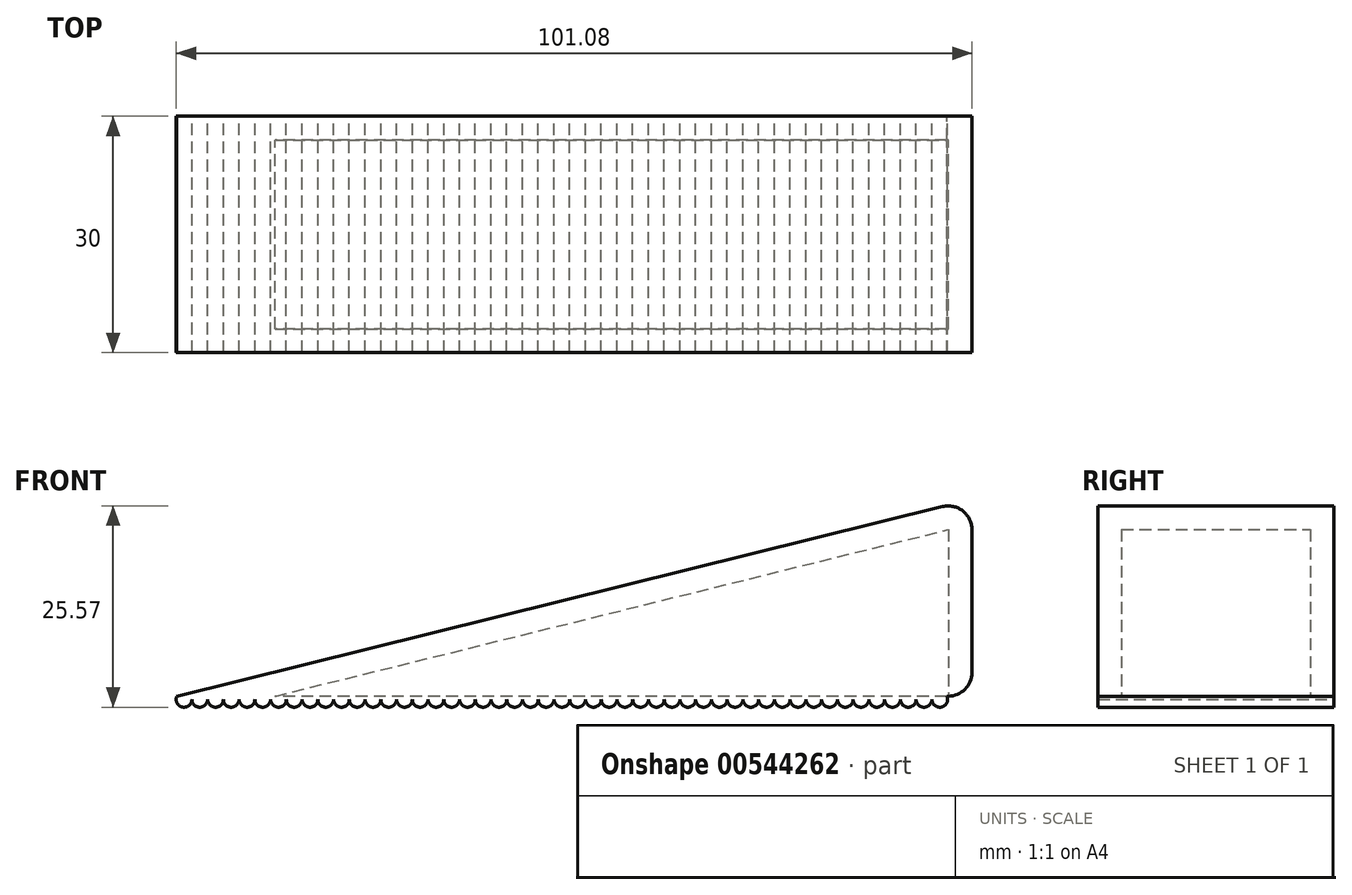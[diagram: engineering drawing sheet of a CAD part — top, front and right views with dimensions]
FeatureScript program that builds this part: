
annotation { "Feature Type Name" : "Feature", "Feature Type Description" : "" }
export const myFeature = defineFeature(function(context is Context, id is Id, definition is map)
    precondition{}
    {
        {
            var Q0;
            Q0=qCreatedBy(makeId("Front.planeOp"),FACE);
            var sketch = newSketch(context, id + "F0", { "sketchPlane" : qUnion([Q0])});
            skLineSegment(sketch, "E0", {"start": v(-3, 0) * mm, "end": v(-101, 0) * mm});
            skLineSegment(sketch, "E1", {"start": v(-101, 0) * mm, "end": v(-3.72, 24.08) * mm});
            skLineSegment(sketch, "E2", {"start": v(0, 21.17) * mm, "end": v(0, 3) * mm});
            skPoint(sketch, "E3.visualSharp", {"position": v(0, 25) * mm});
            skArc(sketch, "E3.filletArc", {"start": v(0, 21.17) * mm, "mid": v(-1.15, 23.53) * mm, "end": v(-3.72, 24.08) * mm});
            skPoint(sketch, "E4.visualSharp", {"position": v(0, 0) * mm});
            skArc(sketch, "E4.filletArc", {"start": v(-3, 0) * mm, "mid": v(-0.88, 0.88) * mm, "end": v(0, 3) * mm});
            skArc(sketch, "E5", {"start": v(-101, 0) * mm, "mid": v(-100.08, -1.4) * mm, "end": v(-99.17, 0) * mm});
            skArc(sketch, "E6.1.0.0", {"start": v(-99, 0) * mm, "mid": v(-98.08, -1.4) * mm, "end": v(-97.17, 0) * mm});
            skArc(sketch, "E6.2.0.0", {"start": v(-97, 0) * mm, "mid": v(-96.08, -1.4) * mm, "end": v(-95.17, 0) * mm});
            skArc(sketch, "E6.3.0.0", {"start": v(-95, 0) * mm, "mid": v(-94.08, -1.4) * mm, "end": v(-93.17, 0) * mm});
            skArc(sketch, "E6.4.0.0", {"start": v(-93, 0) * mm, "mid": v(-92.08, -1.4) * mm, "end": v(-91.17, 0) * mm});
            skArc(sketch, "E6.5.0.0", {"start": v(-91, 0) * mm, "mid": v(-90.08, -1.4) * mm, "end": v(-89.17, 0) * mm});
            skArc(sketch, "E6.6.0.0", {"start": v(-89, 0) * mm, "mid": v(-88.08, -1.4) * mm, "end": v(-87.17, 0) * mm});
            skArc(sketch, "E6.7.0.0", {"start": v(-87, 0) * mm, "mid": v(-86.08, -1.4) * mm, "end": v(-85.17, 0) * mm});
            skArc(sketch, "E6.8.0.0", {"start": v(-85, 0) * mm, "mid": v(-84.08, -1.4) * mm, "end": v(-83.17, 0) * mm});
            skArc(sketch, "E6.9.0.0", {"start": v(-83, 0) * mm, "mid": v(-82.08, -1.4) * mm, "end": v(-81.17, 0) * mm});
            skArc(sketch, "E6.10.0.0", {"start": v(-81, 0) * mm, "mid": v(-80.08, -1.4) * mm, "end": v(-79.17, 0) * mm});
            skArc(sketch, "E6.11.0.0", {"start": v(-79, 0) * mm, "mid": v(-78.08, -1.4) * mm, "end": v(-77.17, 0) * mm});
            skArc(sketch, "E6.12.0.0", {"start": v(-77, 0) * mm, "mid": v(-76.08, -1.4) * mm, "end": v(-75.17, 0) * mm});
            skArc(sketch, "E6.13.0.0", {"start": v(-75, 0) * mm, "mid": v(-74.08, -1.4) * mm, "end": v(-73.17, 0) * mm});
            skArc(sketch, "E6.14.0.0", {"start": v(-73, 0) * mm, "mid": v(-72.08, -1.4) * mm, "end": v(-71.17, 0) * mm});
            skArc(sketch, "E6.15.0.0", {"start": v(-71, 0) * mm, "mid": v(-70.08, -1.4) * mm, "end": v(-69.17, 0) * mm});
            skArc(sketch, "E6.16.0.0", {"start": v(-69, 0) * mm, "mid": v(-68.08, -1.4) * mm, "end": v(-67.17, 0) * mm});
            skArc(sketch, "E6.17.0.0", {"start": v(-67, 0) * mm, "mid": v(-66.08, -1.4) * mm, "end": v(-65.17, 0) * mm});
            skArc(sketch, "E6.18.0.0", {"start": v(-65, 0) * mm, "mid": v(-64.08, -1.4) * mm, "end": v(-63.17, 0) * mm});
            skArc(sketch, "E6.19.0.0", {"start": v(-63, 0) * mm, "mid": v(-62.08, -1.4) * mm, "end": v(-61.17, 0) * mm});
            skArc(sketch, "E6.20.0.0", {"start": v(-61, 0) * mm, "mid": v(-60.08, -1.4) * mm, "end": v(-59.17, 0) * mm});
            skArc(sketch, "E6.21.0.0", {"start": v(-59, 0) * mm, "mid": v(-58.08, -1.4) * mm, "end": v(-57.17, 0) * mm});
            skArc(sketch, "E6.22.0.0", {"start": v(-57, 0) * mm, "mid": v(-56.08, -1.4) * mm, "end": v(-55.17, 0) * mm});
            skArc(sketch, "E6.23.0.0", {"start": v(-55, 0) * mm, "mid": v(-54.08, -1.4) * mm, "end": v(-53.17, 0) * mm});
            skArc(sketch, "E6.24.0.0", {"start": v(-53, 0) * mm, "mid": v(-52.08, -1.4) * mm, "end": v(-51.17, 0) * mm});
            skArc(sketch, "E6.25.0.0", {"start": v(-51, 0) * mm, "mid": v(-50.08, -1.4) * mm, "end": v(-49.17, 0) * mm});
            skArc(sketch, "E6.26.0.0", {"start": v(-49, 0) * mm, "mid": v(-48.08, -1.4) * mm, "end": v(-47.17, 0) * mm});
            skArc(sketch, "E6.27.0.0", {"start": v(-47, 0) * mm, "mid": v(-46.08, -1.4) * mm, "end": v(-45.17, 0) * mm});
            skArc(sketch, "E6.28.0.0", {"start": v(-45, 0) * mm, "mid": v(-44.08, -1.4) * mm, "end": v(-43.17, 0) * mm});
            skArc(sketch, "E6.29.0.0", {"start": v(-43, 0) * mm, "mid": v(-42.08, -1.4) * mm, "end": v(-41.17, 0) * mm});
            skArc(sketch, "E6.30.0.0", {"start": v(-41, 0) * mm, "mid": v(-40.08, -1.4) * mm, "end": v(-39.17, 0) * mm});
            skArc(sketch, "E6.31.0.0", {"start": v(-39, 0) * mm, "mid": v(-38.08, -1.4) * mm, "end": v(-37.17, 0) * mm});
            skArc(sketch, "E6.32.0.0", {"start": v(-37, 0) * mm, "mid": v(-36.08, -1.4) * mm, "end": v(-35.17, 0) * mm});
            skArc(sketch, "E6.33.0.0", {"start": v(-35, 0) * mm, "mid": v(-34.08, -1.4) * mm, "end": v(-33.17, 0) * mm});
            skArc(sketch, "E6.34.0.0", {"start": v(-33, 0) * mm, "mid": v(-32.08, -1.4) * mm, "end": v(-31.17, 0) * mm});
            skArc(sketch, "E6.35.0.0", {"start": v(-31, 0) * mm, "mid": v(-30.08, -1.4) * mm, "end": v(-29.17, 0) * mm});
            skArc(sketch, "E6.36.0.0", {"start": v(-29, 0) * mm, "mid": v(-28.08, -1.4) * mm, "end": v(-27.17, 0) * mm});
            skArc(sketch, "E6.37.0.0", {"start": v(-27, 0) * mm, "mid": v(-26.08, -1.4) * mm, "end": v(-25.17, 0) * mm});
            skArc(sketch, "E6.38.0.0", {"start": v(-25, 0) * mm, "mid": v(-24.08, -1.4) * mm, "end": v(-23.17, 0) * mm});
            skArc(sketch, "E6.39.0.0", {"start": v(-23, 0) * mm, "mid": v(-22.08, -1.4) * mm, "end": v(-21.17, 0) * mm});
            skArc(sketch, "E6.40.0.0", {"start": v(-21, 0) * mm, "mid": v(-20.08, -1.4) * mm, "end": v(-19.17, 0) * mm});
            skArc(sketch, "E6.41.0.0", {"start": v(-19, 0) * mm, "mid": v(-18.08, -1.4) * mm, "end": v(-17.17, 0) * mm});
            skArc(sketch, "E6.42.0.0", {"start": v(-17, 0) * mm, "mid": v(-16.08, -1.4) * mm, "end": v(-15.17, 0) * mm});
            skArc(sketch, "E6.43.0.0", {"start": v(-15, 0) * mm, "mid": v(-14.08, -1.4) * mm, "end": v(-13.17, 0) * mm});
            skArc(sketch, "E6.44.0.0", {"start": v(-13, 0) * mm, "mid": v(-12.08, -1.4) * mm, "end": v(-11.17, 0) * mm});
            skArc(sketch, "E6.45.0.0", {"start": v(-11, 0) * mm, "mid": v(-10.08, -1.4) * mm, "end": v(-9.17, 0) * mm});
            skArc(sketch, "E6.46.0.0", {"start": v(-9, 0) * mm, "mid": v(-8.08, -1.4) * mm, "end": v(-7.17, 0) * mm});
            skArc(sketch, "E6.47.0.0", {"start": v(-7, 0) * mm, "mid": v(-6.08, -1.4) * mm, "end": v(-5.17, 0) * mm});
            skArc(sketch, "E6.48.0.0", {"start": v(-5, 0) * mm, "mid": v(-4.08, -1.4) * mm, "end": v(-3.17, 0) * mm});
            skLineSegment(sketch, "E6.direction1", {"start": v(-101, 0) * mm, "end": v(-99, 0) * mm, "construction": true});
            skSolve(sketch);
        }
        {
            var Q0;
            Q0 = qSketchRegion(id + "F0", true);
            extrude(context, id + "F1", {"entities" : qUnion([Q0]), "endBound" : BoundingType.SYMMETRIC, "depth" : 30 * mm, "offsetDistance" : 25 * mm});
        }
        {
            var Q0;
            Q0=makeQuery(id+"F1.opExtrude","SWEPT_FACE",FACE,{"disambiguationData":[OSD([sQuery(id+"F0.wireOp",EDGE,"E0")])]});
            shell(context, id + "F2", {"entities" : qUnion([Q0]), "thickness" : 3 * mm});
        }
    });
